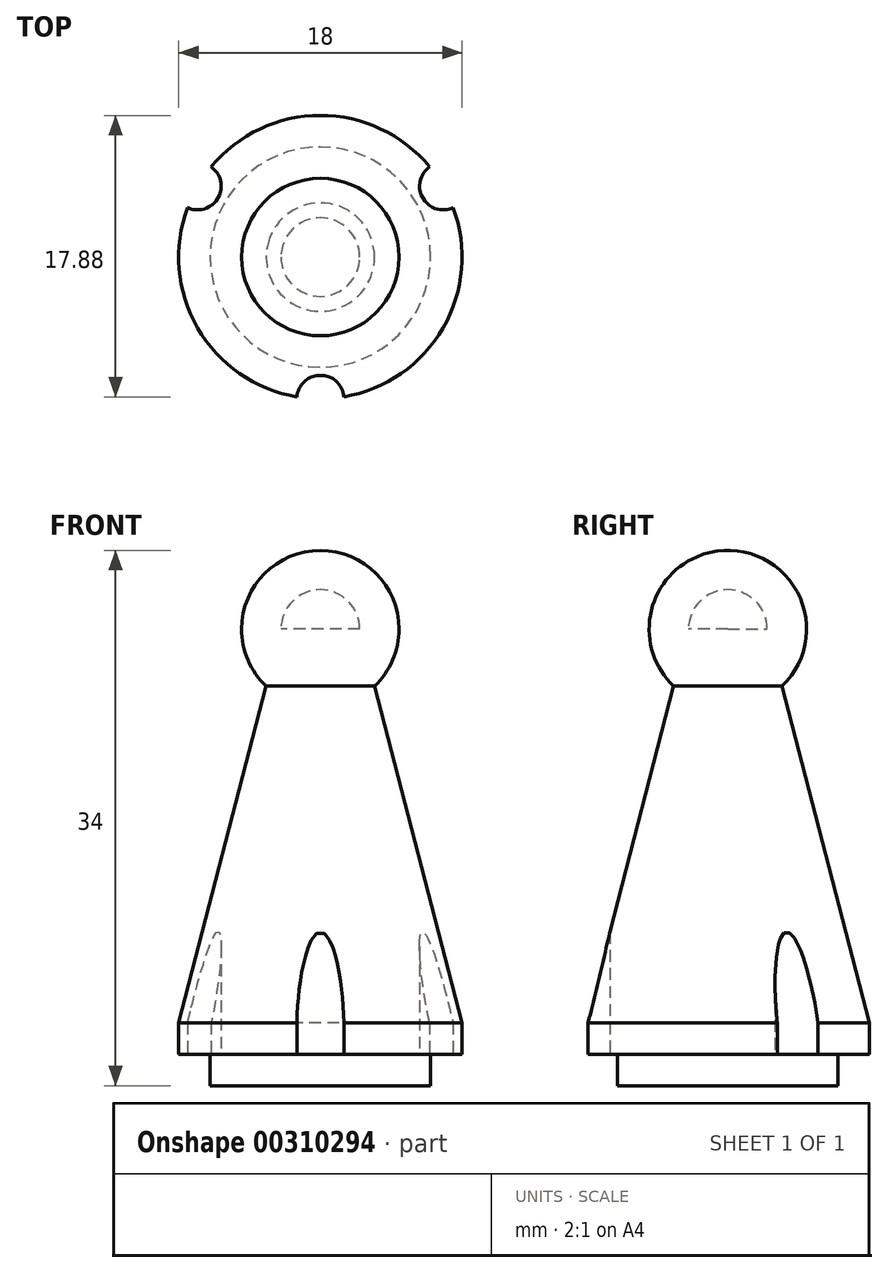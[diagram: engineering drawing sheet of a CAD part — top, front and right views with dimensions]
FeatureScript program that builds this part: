
annotation { "Feature Type Name" : "Feature", "Feature Type Description" : "" }
export const myFeature = defineFeature(function(context is Context, id is Id, definition is map)
    precondition{}
    {
        {
            var Q0;
            Q0=qCreatedBy(makeId("Top.planeOp"),FACE);
            var sketch = newSketch(context, id + "F0", { "sketchPlane" : qUnion([Q0])});
            skCircle(sketch, "E0", {"center": v(0, 0) * mm, "radius": 7 * mm});
            skSolve(sketch);
        }
        {
            var Q0;
            Q0 = qSketchRegion(id + "F0", true);
            extrude(context, id + "F1", {"entities" : qUnion([Q0]), "depth" : 2 * mm});
        }
        {
            var Q0;
            Q0=makeQuery(id+"F1.opExtrude","CAP_FACE",FACE,{"disambiguationData":[OSD([sQuery(id+"F0.wireOp",EDGE,"E0")])],"isStart":false});
            var sketch = newSketch(context, id + "F2", { "sketchPlane" : qUnion([Q0])});
            skCircle(sketch, "E1", {"center": v(0, 0) * mm, "radius": 9 * mm});
            skSolve(sketch);
        }
        {
            var Q0;
            Q0 = qSketchRegion(id + "F2", true);
            extrude(context, id + "F3", {"entities" : qUnion([Q0]), "operationType" : NewBodyOperationType.ADD, "depth" : 2 * mm});
        }
        {
            var Q0;
            Q0=makeQuery(id+"F3.opExtrude","CAP_FACE",FACE,{"disambiguationData":[OSD([sQuery(id+"F2.wireOp",EDGE,"E1")])],"isStart":false});
            cPlane(context, id + "F4", {"entities" : qUnion([Q0]), "cplaneType" : CPlaneType.OFFSET, "offset" : 25 * mm, "width" : 150 * mm, "height" : 150 * mm});
        }
        {
            var Q0;
            Q0=qCreatedBy(id+"F4.planeOp",FACE);
            var sketch = newSketch(context, id + "F5", { "sketchPlane" : qUnion([Q0])});
            skCircle(sketch, "E2", {"center": v(0, 0) * mm, "radius": 2.5 * mm});
            skSolve(sketch);
        }
        {
            var Q1;
            Q1=makeQuery(id+"F5.imprint","IMPRINT",FACE,{"disambiguationData":[TD([[makeQuery(id+"F5.imprint","IMPRINT",EDGE,{"derivedFrom":sQuery(id+"F5.wireOp",EDGE,"E2")}),1.0]])]});
            var Q2;
            Q2=makeQuery(id+"F3.opExtrude","CAP_FACE",FACE,{"disambiguationData":[OSD([sQuery(id+"F2.wireOp",EDGE,"E1")])],"isStart":false});
            loft(context, id + "F6", {"operationType" : NewBodyOperationType.ADD, "sheetProfilesArray" : [{ "sheetProfileEntities" : qUnion([Q1]) }, { "sheetProfileEntities" : qUnion([Q2]) }]});
        }
        {
            var Q0;
            Q0=makeQuery(id+"F5.imprint","IMPRINT",FACE,{"disambiguationData":[TD([[makeQuery(id+"F5.imprint","IMPRINT",EDGE,{"derivedFrom":sQuery(id+"F5.wireOp",EDGE,"E2")}),1.0]])]});
            var sketch = newSketch(context, id + "F7", { "sketchPlane" : qUnion([Q0])});
            skCircle(sketch, "E3", {"center": v(0, 0) * mm, "radius": 5 * mm});
            skLineSegment(sketch, "E4", {"start": v(0, 0) * mm, "end": v(5, 0) * mm});
            skLineSegment(sketch, "E5", {"start": v(5, 0) * mm, "end": v(-5, 0) * mm});
            skSolve(sketch);
        }
        {
            var Q0;
            {var subQ0=sQuery(id+"F7.wireOp",EDGE,"E5");var subQ1=makeQuery(id+"F7.imprint","IMPRINT",VERTEX,{"derivedFrom":subQ0});Q0=makeQuery(id+"F7.imprint","IMPRINT",FACE,{"disambiguationData":[TD([[makeQuery(id+"F7.imprint","IMPRINT",EDGE,{"disambiguationData":[TD([[subQ1,1.0]])],"derivedFrom":subQ0}),-1.0]])]});}
            var Q1;
            {var subQ0=sQuery(id+"F7.wireOp",EDGE,"E5");var subQ1=sQuery(id+"F7.wireOp",EDGE,"E3");var subQ2=makeQuery(id+"F7.imprint","INTERSECT",VERTEX,{"disambiguationData":[OD(0.0)],"derivedFrom":[subQ1,subQ0]});Q1=makeQuery(id+"F7.imprint","IMPRINT",FACE,{"disambiguationData":[TD([[makeQuery(id+"F7.imprint","IMPRINT",EDGE,{"disambiguationData":[TD([[subQ2,-1.0]])],"derivedFrom":subQ1}),1.0]])]});}
            var Q2;
            Q2=sQuery(id+"F7.wireOp",EDGE,"E5");
            revolve(context, id + "F8", {"operationType" : NewBodyOperationType.ADD, "entities" : qUnion([Q0, Q1]), "axis" : qUnion([Q2]), "revolveType" : RevolveType.FULL});
        }
        {
            var Q0;
            Q0=makeQuery(id+"F3.opExtrude","CAP_FACE",FACE,{"disambiguationData":[OSD([sQuery(id+"F2.wireOp",EDGE,"E1")])],"isStart":true});
            var sketch = newSketch(context, id + "F9", { "sketchPlane" : qUnion([Q0])});
            skCircle(sketch, "E6", {"center": v(0, 9) * mm, "radius": 1.5 * mm});
            skCircle(sketch, "E7.1.0", {"center": v(-7.8, -4.5) * mm, "radius": 1.5 * mm});
            skCircle(sketch, "E7.2.0", {"center": v(7.8, -4.5) * mm, "radius": 1.5 * mm});
            skPoint(sketch, "E7.center", {"position": v(0, 0) * mm});
            skSolve(sketch);
        }
        {
            var Q0;
            Q0 = qSketchRegion(id + "F9", true);
            extrude(context, id + "F10", {"entities" : qUnion([Q0]), "operationType" : NewBodyOperationType.REMOVE, "oppositeDirection" : true, "depth" : 10 * mm});
        }
    });
